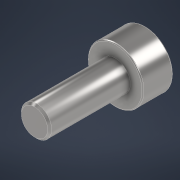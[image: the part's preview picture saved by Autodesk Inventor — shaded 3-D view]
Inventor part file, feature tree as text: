
AUTODESK INVENTOR PART (.ipt)
format: ipt  version: 2022 (Build 260153000, 153)  size: 140,800 bytes
history: native  units: in
note: dims shown in document units (in); Inventor stores cm internally (conversion verified against a paired STEP export)
features: sketch x3, extrude x2, plane x1, fillet x1, chamfer x1
ambient origin geometry x8: Origin, YZ Plane, XZ Plane, XY Plane, X Axis, Y Axis, Z Axis, Center Point
bodies: Body1 (feature_tree)
feature tree (8):
  plane  "Work Plane1"
  fillet  "Fillet1"  [1 undecoded]
  extrude  "Extrusion2"  Depth=0.0039in
  extrude  "Extrusion1"  Depth=0.315in TaperAngle=0.0deg
  chamfer  "Chamfer1"  Distance=0.0079in
  sketch  "Sketch1"  dims[d1=0.1181in d2=0.0in d3=0.0039in]
  sketch  "Sketch2"  dims[d4=0.1181in d5=0.0in d6=0.315in d7=0.0in d8=0.0079in d9=0.0079in d10=17.7165in]
  sketch  "Sketch3"
note: 1 required parameter value undecoded (feature->parameter linkage not recoverable at this tier; creation-order binding heuristic only, values carry confidence <= 0.55)
